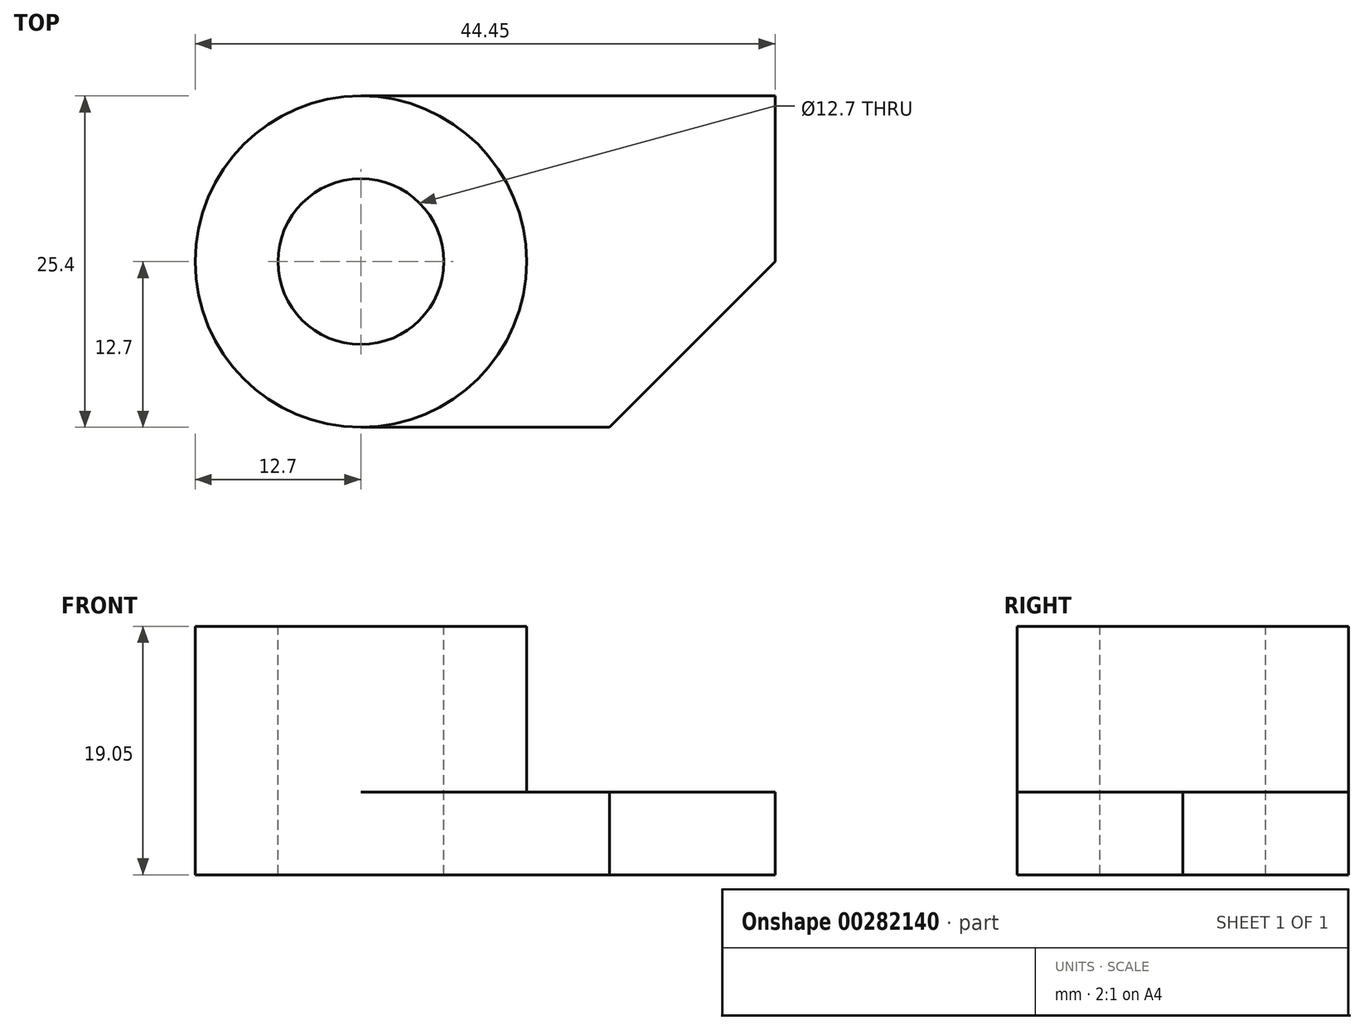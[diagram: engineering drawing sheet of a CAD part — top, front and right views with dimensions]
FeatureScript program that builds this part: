
annotation { "Feature Type Name" : "Feature", "Feature Type Description" : "" }
export const myFeature = defineFeature(function(context is Context, id is Id, definition is map)
    precondition{}
    {
        {
            var Q0;
            Q0=qCreatedBy(makeId("Top.planeOp"),FACE);
            var sketch = newSketch(context, id + "F0", { "sketchPlane" : qUnion([Q0])});
            skLineSegment(sketch, "E0", {"start": v(0, 0) * mm, "end": v(19.05, 0) * mm});
            skLineSegment(sketch, "E1", {"start": v(19.05, 0) * mm, "end": v(31.75, 12.7) * mm});
            skLineSegment(sketch, "E2", {"start": v(31.75, 12.7) * mm, "end": v(31.75, 25.4) * mm});
            skLineSegment(sketch, "E3", {"start": v(31.75, 25.4) * mm, "end": v(0, 25.4) * mm});
            skLineSegment(sketch, "E4", {"start": v(31.75, 12.7) * mm, "end": v(-42.5, 12.7) * mm, "construction": true});
            skCircle(sketch, "E5", {"center": v(0, 12.7) * mm, "radius": 12.7 * mm});
            skCircle(sketch, "E6", {"center": v(0, 12.7) * mm, "radius": 6.35 * mm});
            skSolve(sketch);
        }
        {
            var Q0;
            Q0=makeQuery(id+"F0.imprint","IMPRINT",FACE,{"disambiguationData":[TD([[makeQuery(id+"F0.imprint","IMPRINT",EDGE,{"derivedFrom":sQuery(id+"F0.wireOp",EDGE,"E6")}),-1.0]])]});
            var Q1;
            {var subQ1=sQuery(id+"F0.wireOp",EDGE,"E0");Q1=makeQuery(id+"F0.imprint","IMPRINT",FACE,{"disambiguationData":[TD([[makeQuery(id+"F0.imprint","IMPRINT",EDGE,{"derivedFrom":subQ1}),1.0]])]});}
            extrude(context, id + "F1", {"entities" : qUnion([Q0, Q1]), "oppositeDirection" : true, "depth" : 6.35 * mm});
        }
        {
            var Q0;
            Q0=makeQuery(id+"F0.imprint","IMPRINT",FACE,{"disambiguationData":[TD([[makeQuery(id+"F0.imprint","IMPRINT",EDGE,{"derivedFrom":sQuery(id+"F0.wireOp",EDGE,"E6")}),-1.0]])]});
            extrude(context, id + "F2", {"entities" : qUnion([Q0]), "operationType" : NewBodyOperationType.ADD, "depth" : 12.7 * mm});
        }
    });
